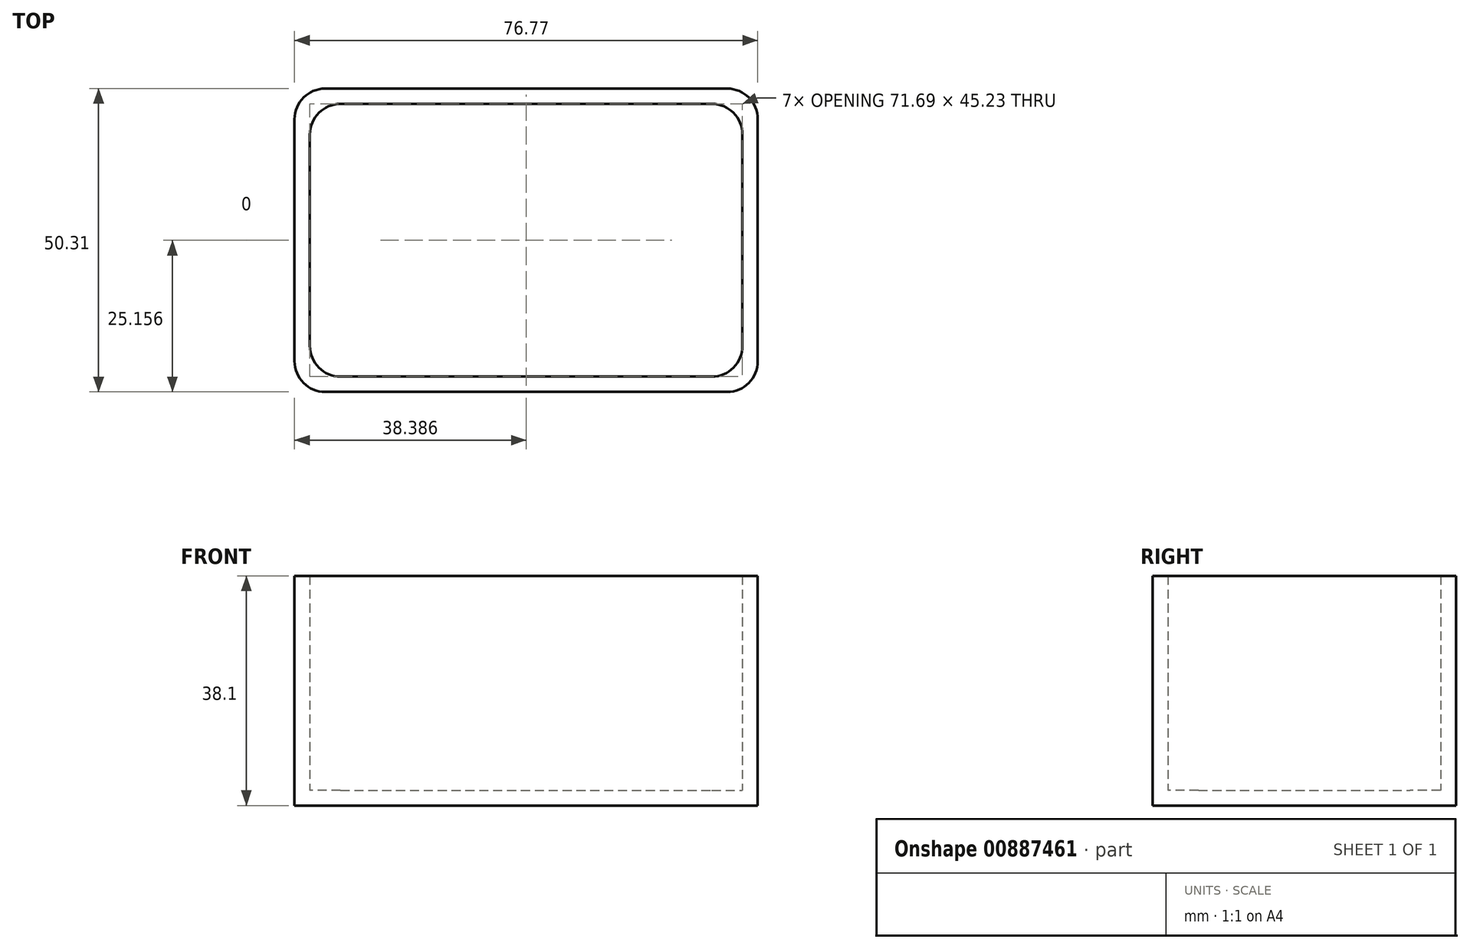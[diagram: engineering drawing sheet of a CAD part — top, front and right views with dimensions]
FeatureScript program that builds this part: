
annotation { "Feature Type Name" : "Feature", "Feature Type Description" : "" }
export const myFeature = defineFeature(function(context is Context, id is Id, definition is map)
    precondition{}
    {
        {
            var Q0;
            Q0=qCreatedBy(makeId("Top.planeOp"),FACE);
            var sketch = newSketch(context, id + "F0", { "sketchPlane" : qUnion([Q0])});
            skLineSegment(sketch, "E0.bottom", {"start": v(0, 0) * mm, "end": v(76.77, 0) * mm});
            skLineSegment(sketch, "E0.top", {"start": v(0, 50.31) * mm, "end": v(76.77, 50.31) * mm});
            skLineSegment(sketch, "E0.left", {"start": v(0, 0) * mm, "end": v(0, 50.31) * mm});
            skLineSegment(sketch, "E0.right", {"start": v(76.77, 0) * mm, "end": v(76.77, 50.31) * mm});
            skSolve(sketch);
        }
        {
            var Q0;
            Q0=makeQuery(id+"F0.imprint","IMPRINT",FACE,{"disambiguationData":[TD([[makeQuery(id+"F0.imprint","IMPRINT",EDGE,{"derivedFrom":sQuery(id+"F0.wireOp",EDGE,"E0.bottom")}),1.0]])]});
            extrude(context, id + "F1", {"entities" : qUnion([Q0]), "depth" : 38.1 * mm, "offsetDistance" : 25.4 * mm});
        }
        {
            var Q0;
            Q0=makeQuery(id+"F1.opExtrude","CAP_FACE",FACE,{"disambiguationData":[OSD([sQuery(id+"F0.wireOp",EDGE,"E0.bottom"),sQuery(id+"F0.wireOp",EDGE,"E0.top"),sQuery(id+"F0.wireOp",EDGE,"E0.left"),sQuery(id+"F0.wireOp",EDGE,"E0.right")])],"isStart":false});
            shell(context, id + "F2", {"entities" : qUnion([Q0]), "thickness" : 2.54 * mm});
        }
        {
            var Q0;
            Q0=makeQuery(id+"F1.opExtrude","SWEPT_EDGE",EDGE,{"disambiguationData":[OSD([sQuery(id+"F0.wireOp",EDGE,"E0.bottom"),sQuery(id+"F0.wireOp",EDGE,"E0.right")])]});
            var Q1;
            Q1=makeQuery(id+"F1.opExtrude","SWEPT_EDGE",EDGE,{"disambiguationData":[OSD([sQuery(id+"F0.wireOp",EDGE,"E0.top"),sQuery(id+"F0.wireOp",EDGE,"E0.right")])]});
            var Q2;
            Q2=makeQuery(id+"F1.opExtrude","SWEPT_EDGE",EDGE,{"disambiguationData":[OSD([sQuery(id+"F0.wireOp",EDGE,"E0.bottom"),sQuery(id+"F0.wireOp",EDGE,"E0.left")])]});
            var Q3;
            Q3=makeQuery(id+"F1.opExtrude","SWEPT_EDGE",EDGE,{"disambiguationData":[OSD([sQuery(id+"F0.wireOp",EDGE,"E0.top"),sQuery(id+"F0.wireOp",EDGE,"E0.left")])]});
            var Q4;
            Q4=makeQuery(id+"F2.opShell","OFFSET_EDGE",EDGE,{"disambiguationData":[OSD([sQuery(id+"F0.wireOp",EDGE,"E0.bottom"),sQuery(id+"F0.wireOp",EDGE,"E0.right")])]});
            var Q5;
            Q5=makeQuery(id+"F2.opShell","OFFSET_EDGE",EDGE,{"disambiguationData":[OSD([sQuery(id+"F0.wireOp",EDGE,"E0.top"),sQuery(id+"F0.wireOp",EDGE,"E0.right")])]});
            var Q6;
            Q6=makeQuery(id+"F2.opShell","OFFSET_EDGE",EDGE,{"disambiguationData":[OSD([sQuery(id+"F0.wireOp",EDGE,"E0.bottom"),sQuery(id+"F0.wireOp",EDGE,"E0.left")])]});
            var Q7;
            Q7=makeQuery(id+"F2.opShell","OFFSET_EDGE",EDGE,{"disambiguationData":[OSD([sQuery(id+"F0.wireOp",EDGE,"E0.top"),sQuery(id+"F0.wireOp",EDGE,"E0.left")])]});
            fillet(context, id + "F3", {"entities" : qUnion([Q0, Q1, Q2, Q3, Q4, Q5, Q6, Q7]), "radius" : 5.08 * mm, "tangentPropagation" : true, "allowEdgeOverflow" : false});
        }
    });
